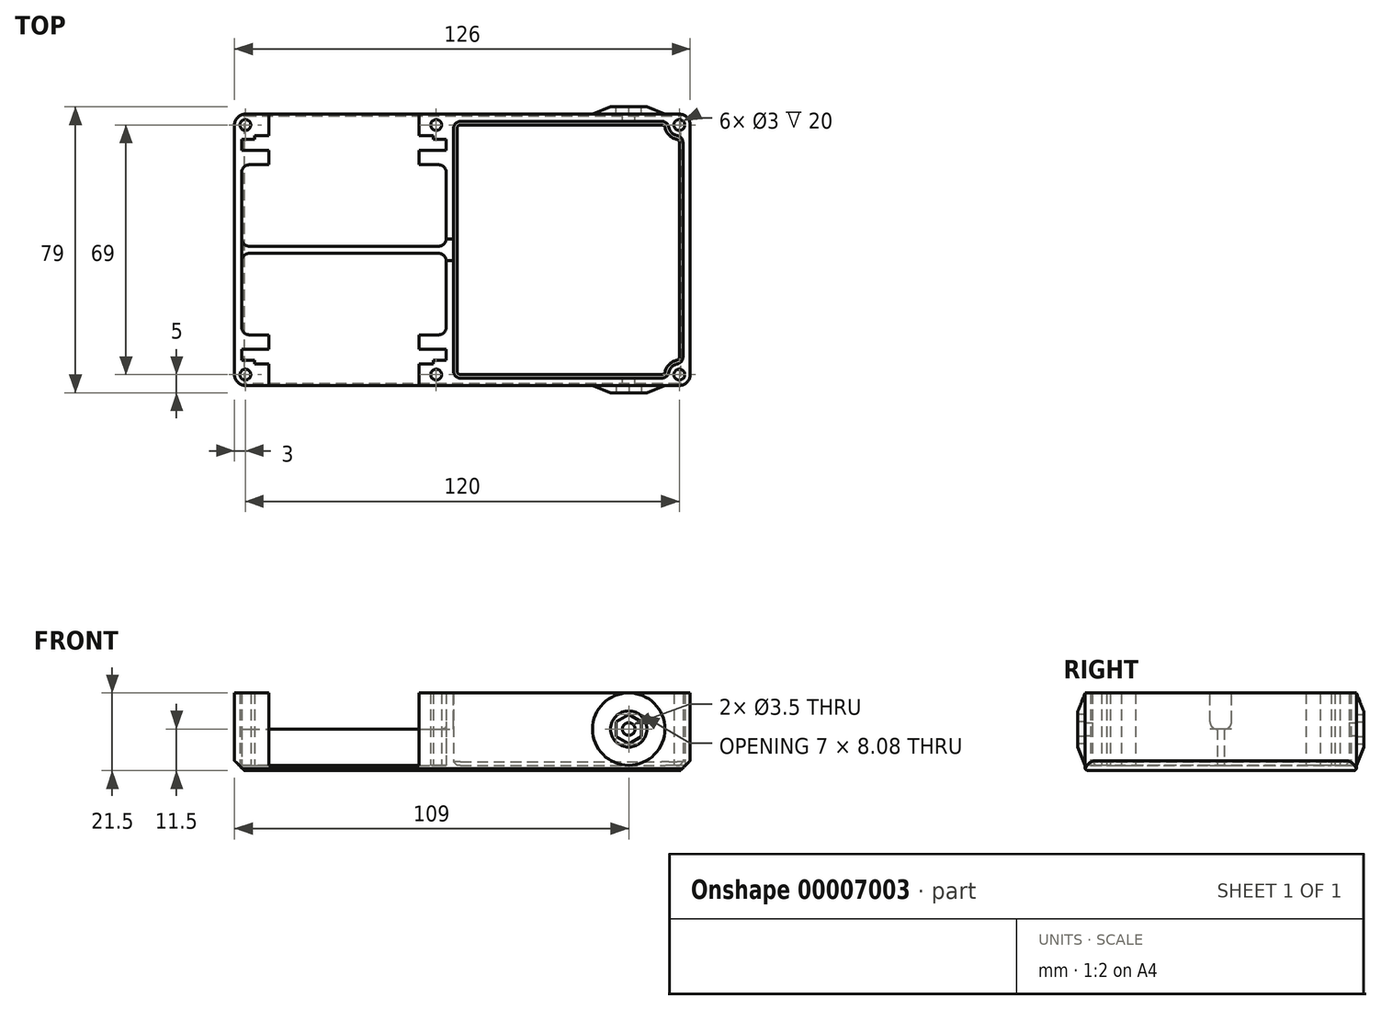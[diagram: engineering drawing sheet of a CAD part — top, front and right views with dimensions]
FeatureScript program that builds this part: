
annotation { "Feature Type Name" : "Feature", "Feature Type Description" : "" }
export const myFeature = defineFeature(function(context is Context, id is Id, definition is map)
    precondition{}
    {
        {
            var Q0;
            Q0=qCreatedBy(makeId("Top.planeOp"),FACE);
            var sketch = newSketch(context, id + "F0", { "sketchPlane" : qUnion([Q0])});
            skLineSegment(sketch, "E0.0", {"start": v(41, 72) * mm, "end": v(41, 66) * mm});
            skLineSegment(sketch, "E1.0", {"start": v(-7.5, 62) * mm, "end": v(-0.5, 62) * mm});
            skLineSegment(sketch, "E2.0", {"start": v(-8, 65) * mm, "end": v(-8, 62.5) * mm});
            skLineSegment(sketch, "E3.0", {"start": v(41, 62) * mm, "end": v(48, 62) * mm});
            skLineSegment(sketch, "E4.0", {"start": v(48.5, 62.5) * mm, "end": v(48.5, 65) * mm});
            skLineSegment(sketch, "E5.trimOffspring", {"start": v(-0.5, 66) * mm, "end": v(-0.5, 72) * mm});
            skLineSegment(sketch, "E6", {"start": v(-8, 62.5) * mm, "end": v(-8, 62) * mm});
            skLineSegment(sketch, "E7", {"start": v(-8, 62) * mm, "end": v(-7.5, 62) * mm});
            skLineSegment(sketch, "E8", {"start": v(48, 62) * mm, "end": v(48.5, 62) * mm});
            skLineSegment(sketch, "E9", {"start": v(48.5, 62) * mm, "end": v(48.5, 62.5) * mm});
            skLineSegment(sketch, "E10", {"start": v(45, 65) * mm, "end": v(48.5, 65) * mm});
            skLineSegment(sketch, "E11", {"start": v(-8, 65) * mm, "end": v(-4.5, 65) * mm});
            skLineSegment(sketch, "E12", {"start": v(-0.5, 66) * mm, "end": v(-4.5, 66) * mm});
            skLineSegment(sketch, "E13", {"start": v(-4.5, 66) * mm, "end": v(-4.5, 65) * mm});
            skLineSegment(sketch, "E14", {"start": v(41, 66) * mm, "end": v(45, 66) * mm});
            skLineSegment(sketch, "E15", {"start": v(45, 66) * mm, "end": v(45, 65) * mm});
            skLineSegment(sketch, "E16", {"start": v(-0.5, 62) * mm, "end": v(-0.5, 58) * mm});
            skLineSegment(sketch, "E17", {"start": v(41, 62) * mm, "end": v(41, 58) * mm});
            skLineSegment(sketch, "E18", {"start": v(-0.5, 58) * mm, "end": v(-8, 58) * mm});
            skLineSegment(sketch, "E19", {"start": v(41, 58) * mm, "end": v(48.5, 58) * mm});
            skLineSegment(sketch, "E20", {"start": v(-0.5, 72) * mm, "end": v(-10, 72) * mm});
            skLineSegment(sketch, "E21", {"start": v(41, 72) * mm, "end": v(116, 72) * mm});
            skLineSegment(sketch, "E22.1", {"start": v(50.5, 70) * mm, "end": v(110.17, 70) * mm});
            skPoint(sketch, "E23.endSnap0", {"position": v(41, 69) * mm});
            skCircle(sketch, "E24", {"center": v(45.75, 69) * mm, "radius": 1.5 * mm});
            skCircle(sketch, "E25", {"center": v(-7, 69) * mm, "radius": 1.5 * mm});
            skCircle(sketch, "E26", {"center": v(113, 69) * mm, "radius": 1.5 * mm});
            skArc(sketch, "E27.trimOffspring", {"start": v(110.17, 70) * mm, "mid": v(110.88, 66.88) * mm, "end": v(114, 66.17) * mm});
            skLineSegment(sketch, "E28", {"start": v(-8, 58) * mm, "end": v(-8, 35.5) * mm});
            skLineSegment(sketch, "E29", {"start": v(-8, 35.5) * mm, "end": v(48.5, 35.5) * mm});
            skLineSegment(sketch, "E30", {"start": v(48.5, 35.5) * mm, "end": v(48.5, 58) * mm});
            skLineSegment(sketch, "E31.MirrorCS", {"start": v(-8, 7) * mm, "end": v(-7.5, 7) * mm});
            skLineSegment(sketch, "E32.MirrorCS", {"start": v(48.5, 6.5) * mm, "end": v(48.5, 4) * mm});
            skLineSegment(sketch, "E33.MirrorCS", {"start": v(-8, 4) * mm, "end": v(-8, 6.5) * mm});
            skLineSegment(sketch, "E34.MirrorCS", {"start": v(-4.5, 3) * mm, "end": v(-4.5, 4) * mm});
            skLineSegment(sketch, "E35.MirrorCS", {"start": v(-0.5, 7) * mm, "end": v(-0.5, 11) * mm});
            skLineSegment(sketch, "E36.MirrorCS", {"start": v(-0.5, 3) * mm, "end": v(-4.5, 3) * mm});
            skCircle(sketch, "E37.MirrorC", {"center": v(113, 0) * mm, "radius": 1.5 * mm});
            skCircle(sketch, "E38.MirrorC", {"center": v(-7, 0) * mm, "radius": 1.5 * mm});
            skLineSegment(sketch, "E39.MirrorCS", {"start": v(45, 4) * mm, "end": v(48.5, 4) * mm});
            skLineSegment(sketch, "E40.MirrorCS", {"start": v(45, 3) * mm, "end": v(45, 4) * mm});
            skLineSegment(sketch, "E41.MirrorCS", {"start": v(-8, 4) * mm, "end": v(-4.5, 4) * mm});
            skLineSegment(sketch, "E42.MirrorCS", {"start": v(41, 7) * mm, "end": v(41, 11) * mm});
            skLineSegment(sketch, "E43.MirrorCS", {"start": v(41, 3) * mm, "end": v(45, 3) * mm});
            skLineSegment(sketch, "E44.MirrorCS", {"start": v(-0.5, -3) * mm, "end": v(-10, -3) * mm});
            skArc(sketch, "E45.MirrorCS", {"start": v(110.17, -1) * mm, "mid": v(110.88, 2.12) * mm, "end": v(114, 2.83) * mm});
            skCircle(sketch, "E46.MirrorC", {"center": v(45.75, 0) * mm, "radius": 1.5 * mm});
            skLineSegment(sketch, "E47.MirrorCS", {"start": v(-7.5, 7) * mm, "end": v(-0.5, 7) * mm});
            skLineSegment(sketch, "E48.MirrorCS", {"start": v(41, -3) * mm, "end": v(41, 3) * mm});
            skLineSegment(sketch, "E49.MirrorCS", {"start": v(-8, 33.5) * mm, "end": v(48.5, 33.5) * mm});
            skLineSegment(sketch, "E50.MirrorCS", {"start": v(41, 7) * mm, "end": v(48, 7) * mm});
            skLineSegment(sketch, "E51.MirrorCS", {"start": v(48.5, 33.5) * mm, "end": v(48.5, 11) * mm});
            skLineSegment(sketch, "E52.MirrorCS", {"start": v(-0.5, 3) * mm, "end": v(-0.5, -3) * mm});
            skPoint(sketch, "E53.MirrorP", {"position": v(41, 0) * mm});
            skLineSegment(sketch, "E54.MirrorCS", {"start": v(-0.5, 11) * mm, "end": v(-8, 11) * mm});
            skLineSegment(sketch, "E55.MirrorCS", {"start": v(41, 11) * mm, "end": v(48.5, 11) * mm});
            skLineSegment(sketch, "E56.MirrorCS", {"start": v(41, -3) * mm, "end": v(116, -3) * mm});
            skLineSegment(sketch, "E57.MirrorCS", {"start": v(-8, 11) * mm, "end": v(-8, 33.5) * mm});
            skLineSegment(sketch, "E58.MirrorCS", {"start": v(50.5, -1) * mm, "end": v(110.17, -1) * mm});
            skLineSegment(sketch, "E59", {"start": v(116, 72) * mm, "end": v(116, -3) * mm});
            skLineSegment(sketch, "E60", {"start": v(114, 2.83) * mm, "end": v(114, 66.17) * mm});
            skLineSegment(sketch, "E61", {"start": v(-10, 72) * mm, "end": v(-10, -3) * mm});
            skLineSegment(sketch, "E62", {"start": v(-8, 7) * mm, "end": v(-8, 6.5) * mm});
            skLineSegment(sketch, "E63", {"start": v(48, 7) * mm, "end": v(48.5, 7) * mm});
            skLineSegment(sketch, "E64", {"start": v(48.5, 7) * mm, "end": v(48.5, 6.5) * mm});
            skLineSegment(sketch, "E65", {"start": v(50.5, 70) * mm, "end": v(50.5, -1) * mm});
            skSolve(sketch);
        }
        {
            var Q0;
            Q0=makeQuery(id+"F0.imprint","IMPRINT",FACE,{"disambiguationData":[TD([[makeQuery(id+"F0.imprint","IMPRINT",EDGE,{"derivedFrom":sQuery(id+"F0.wireOp",EDGE,"E0.0")}),1.0]])]});
            extrude(context, id + "F1", {"entities" : qUnion([Q0]), "depth" : 20 * mm});
        }
        {
            var Q0;
            Q0=makeQuery(id+"F1.opExtrude","SWEPT_FACE",FACE,{"disambiguationData":[OSD([sQuery(id+"F0.wireOp",EDGE,"E21")])]});
            var sketch = newSketch(context, id + "F2", { "sketchPlane" : qUnion([Q0])});
            skCircle(sketch, "E66", {"center": v(-99, 10) * mm, "radius": 10 * mm});
            skPoint(sketch, "E66.centerSnap0", {"position": v(-113, 10) * mm});
            skSolve(sketch);
        }
        {
            var Q0;
            Q0 = qSketchRegion(id + "F2", true);
            extrude(context, id + "F3", {"entities" : qUnion([Q0]), "operationType" : NewBodyOperationType.ADD, "depth" : 2 * mm});
        }
        {
            var Q0;
            Q0=makeQuery(id+"F3.opExtrude","CAP_EDGE",EDGE,{"disambiguationData":[OSD([sQuery(id+"F2.wireOp",EDGE,"E66")])],"isStart":false});
            chamfer(context, id + "F4", {"entities" : qUnion([Q0]), "chamferType" : ChamferType.TWO_OFFSETS, "width1" : 5 * mm, "oppositeDirection" : false, "width2" : 2 * mm, "tangentPropagation" : true});
        }
        {
            var Q0;
            Q0=makeQuery(id+"F3.opExtrude","CAP_FACE",FACE,{"disambiguationData":[OSD([sQuery(id+"F2.wireOp",EDGE,"E66")])],"isStart":false});
            var sketch = newSketch(context, id + "F5", { "sketchPlane" : qUnion([Q0])});
            skCircle(sketch, "E67", {"center": v(-99, 10) * mm, "radius": 1.75 * mm});
            skSolve(sketch);
        }
        {
            var Q0;
            Q0=makeQuery(id+"F1.opExtrude","SWEPT_FACE",FACE,{"disambiguationData":[OSD([sQuery(id+"F0.wireOp",EDGE,"E56.MirrorCS")])]});
            var sketch = newSketch(context, id + "F6", { "sketchPlane" : qUnion([Q0])});
            skCircle(sketch, "E68", {"center": v(99, 10) * mm, "radius": 10 * mm});
            skSolve(sketch);
        }
        {
            var Q0;
            Q0 = qSketchRegion(id + "F6", true);
            extrude(context, id + "F7", {"entities" : qUnion([Q0]), "operationType" : NewBodyOperationType.ADD, "depth" : 2 * mm});
        }
        {
            var Q0;
            Q0=makeQuery(id+"F5.imprint","IMPRINT",FACE,{"disambiguationData":[TD([[makeQuery(id+"F5.imprint","IMPRINT",EDGE,{"derivedFrom":sQuery(id+"F5.wireOp",EDGE,"E67")}),1.0]])]});
            extrude(context, id + "F8", {"entities" : qUnion([Q0]), "operationType" : NewBodyOperationType.REMOVE, "oppositeDirection" : true, "depth" : 100 * mm});
        }
        {
            var Q0;
            Q0=makeQuery(id+"F7.opExtrude","CAP_EDGE",EDGE,{"disambiguationData":[OSD([sQuery(id+"F6.wireOp",EDGE,"E68")])],"isStart":false});
            chamfer(context, id + "F9", {"entities" : qUnion([Q0]), "chamferType" : ChamferType.TWO_OFFSETS, "width1" : 5 * mm, "oppositeDirection" : false, "width2" : 2 * mm, "tangentPropagation" : true});
        }
        {
            var Q0;
            Q0=makeQuery(id+"F1.opExtrude","SWEPT_EDGE",EDGE,{"disambiguationData":[OSD([sQuery(id+"F0.wireOp",EDGE,"E44.MirrorCS"),sQuery(id+"F0.wireOp",EDGE,"E61")])]});
            var Q1;
            Q1=makeQuery(id+"F1.opExtrude","SWEPT_EDGE",EDGE,{"disambiguationData":[OSD([sQuery(id+"F0.wireOp",EDGE,"E56.MirrorCS"),sQuery(id+"F0.wireOp",EDGE,"E59")])]});
            var Q2;
            Q2=makeQuery(id+"F1.opExtrude","SWEPT_EDGE",EDGE,{"disambiguationData":[OSD([sQuery(id+"F0.wireOp",EDGE,"E21"),sQuery(id+"F0.wireOp",EDGE,"E59")])]});
            var Q3;
            Q3=makeQuery(id+"F1.opExtrude","SWEPT_EDGE",EDGE,{"disambiguationData":[OSD([sQuery(id+"F0.wireOp",EDGE,"E20"),sQuery(id+"F0.wireOp",EDGE,"E61")])]});
            fillet(context, id + "F10", {"entities" : qUnion([Q0, Q1, Q2, Q3]), "radius" : 3 * mm, "tangentPropagation" : true, "allowEdgeOverflow" : false});
        }
        {
            var Q0;
            Q0=makeQuery(id+"F1.opExtrude","SWEPT_EDGE",EDGE,{"disambiguationData":[OSD([sQuery(id+"F0.wireOp",EDGE,"E45.MirrorCS"),sQuery(id+"F0.wireOp",EDGE,"E58.MirrorCS")])]});
            var Q1;
            Q1=makeQuery(id+"F1.opExtrude","SWEPT_EDGE",EDGE,{"disambiguationData":[OSD([sQuery(id+"F0.wireOp",EDGE,"E45.MirrorCS"),sQuery(id+"F0.wireOp",EDGE,"E60")])]});
            var Q2;
            Q2=makeQuery(id+"F1.opExtrude","SWEPT_EDGE",EDGE,{"disambiguationData":[OSD([sQuery(id+"F0.wireOp",EDGE,"E58.MirrorCS"),sQuery(id+"F0.wireOp",EDGE,"E65")])]});
            var Q3;
            Q3=makeQuery(id+"F1.opExtrude","SWEPT_EDGE",EDGE,{"disambiguationData":[OSD([sQuery(id+"F0.wireOp",EDGE,"E22.1"),sQuery(id+"F0.wireOp",EDGE,"E65")])]});
            var Q4;
            Q4=makeQuery(id+"F1.opExtrude","SWEPT_EDGE",EDGE,{"disambiguationData":[OSD([sQuery(id+"F0.wireOp",EDGE,"E22.1"),sQuery(id+"F0.wireOp",EDGE,"E27.trimOffspring")])]});
            var Q5;
            Q5=makeQuery(id+"F1.opExtrude","SWEPT_EDGE",EDGE,{"disambiguationData":[OSD([sQuery(id+"F0.wireOp",EDGE,"E27.trimOffspring"),sQuery(id+"F0.wireOp",EDGE,"E60")])]});
            var Q6;
            Q6=makeQuery(id+"F1.opExtrude","SWEPT_EDGE",EDGE,{"disambiguationData":[OSD([sQuery(id+"F0.wireOp",EDGE,"E49.MirrorCS"),sQuery(id+"F0.wireOp",EDGE,"E57.MirrorCS")])]});
            var Q7;
            Q7=makeQuery(id+"F1.opExtrude","SWEPT_EDGE",EDGE,{"disambiguationData":[OSD([sQuery(id+"F0.wireOp",EDGE,"E28"),sQuery(id+"F0.wireOp",EDGE,"E29")])]});
            var Q8;
            Q8=makeQuery(id+"F1.opExtrude","SWEPT_EDGE",EDGE,{"disambiguationData":[OSD([sQuery(id+"F0.wireOp",EDGE,"E29"),sQuery(id+"F0.wireOp",EDGE,"E30")])]});
            var Q9;
            Q9=makeQuery(id+"F1.opExtrude","SWEPT_EDGE",EDGE,{"disambiguationData":[OSD([sQuery(id+"F0.wireOp",EDGE,"E49.MirrorCS"),sQuery(id+"F0.wireOp",EDGE,"E51.MirrorCS")])]});
            var Q10;
            Q10=makeQuery(id+"F1.opExtrude","SWEPT_EDGE",EDGE,{"disambiguationData":[OSD([sQuery(id+"F0.wireOp",EDGE,"E19"),sQuery(id+"F0.wireOp",EDGE,"E30")])]});
            var Q11;
            Q11=makeQuery(id+"F1.opExtrude","SWEPT_EDGE",EDGE,{"disambiguationData":[OSD([sQuery(id+"F0.wireOp",EDGE,"E18"),sQuery(id+"F0.wireOp",EDGE,"E28")])]});
            var Q12;
            Q12=makeQuery(id+"F1.opExtrude","SWEPT_EDGE",EDGE,{"disambiguationData":[OSD([sQuery(id+"F0.wireOp",EDGE,"E54.MirrorCS"),sQuery(id+"F0.wireOp",EDGE,"E57.MirrorCS")])]});
            var Q13;
            Q13=makeQuery(id+"F1.opExtrude","SWEPT_EDGE",EDGE,{"disambiguationData":[OSD([sQuery(id+"F0.wireOp",EDGE,"E51.MirrorCS"),sQuery(id+"F0.wireOp",EDGE,"E55.MirrorCS")])]});
            fillet(context, id + "F11", {"entities" : qUnion([Q0, Q1, Q2, Q3, Q4, Q5, Q6, Q7, Q8, Q9, Q10, Q11, Q12, Q13]), "radius" : 2 * mm, "tangentPropagation" : true, "allowEdgeOverflow" : false});
        }
        {
            var Q0;
            Q0=makeQuery(id+"F3.opExtrude","CAP_FACE",FACE,{"disambiguationData":[OSD([sQuery(id+"F2.wireOp",EDGE,"E66")])],"isStart":false});
            var sketch = newSketch(context, id + "F12", { "sketchPlane" : qUnion([Q0])});
            skCircle(sketch, "E69.cCircle", {"center": v(-99, 10) * mm, "radius": 3.5 * mm, "construction": true});
            skLineSegment(sketch, "E69.0", {"start": v(-95.5, 12.02) * mm, "end": v(-95.5, 7.98) * mm});
            skLineSegment(sketch, "E69.1", {"start": v(-95.5, 7.98) * mm, "end": v(-99, 5.96) * mm});
            skLineSegment(sketch, "E69.2", {"start": v(-99, 5.96) * mm, "end": v(-102.5, 7.98) * mm});
            skLineSegment(sketch, "E69.3", {"start": v(-102.5, 7.98) * mm, "end": v(-102.5, 12.02) * mm});
            skLineSegment(sketch, "E69.4", {"start": v(-102.5, 12.02) * mm, "end": v(-99, 14.04) * mm});
            skLineSegment(sketch, "E69.5", {"start": v(-99, 14.04) * mm, "end": v(-95.5, 12.02) * mm});
            skPoint(sketch, "E69.0.midPoint", {"position": v(-95.5, 10) * mm});
            skSolve(sketch);
        }
        {
            var Q0;
            Q0=makeQuery(id+"F12.imprint","IMPRINT",FACE,{"disambiguationData":[TD([[makeQuery(id+"F12.imprint","IMPRINT",EDGE,{"derivedFrom":sQuery(id+"F12.wireOp",EDGE,"E69.0")}),-1.0]])]});
            extrude(context, id + "F13", {"entities" : qUnion([Q0]), "operationType" : NewBodyOperationType.REMOVE, "oppositeDirection" : true, "depth" : 2 * mm});
        }
        {
            var Q0;
            Q0=makeQuery(id+"F7.opExtrude","CAP_FACE",FACE,{"disambiguationData":[OSD([sQuery(id+"F6.wireOp",EDGE,"E68")])],"isStart":false});
            var sketch = newSketch(context, id + "F14", { "sketchPlane" : qUnion([Q0])});
            skCircle(sketch, "E70.cCircle", {"center": v(99, 10) * mm, "radius": 3.5 * mm, "construction": true});
            skLineSegment(sketch, "E70.0", {"start": v(95.5, 7.98) * mm, "end": v(95.5, 12.02) * mm});
            skLineSegment(sketch, "E70.1", {"start": v(95.5, 12.02) * mm, "end": v(99, 14.04) * mm});
            skLineSegment(sketch, "E70.2", {"start": v(99, 14.04) * mm, "end": v(102.5, 12.02) * mm});
            skLineSegment(sketch, "E70.3", {"start": v(102.5, 12.02) * mm, "end": v(102.5, 7.98) * mm});
            skLineSegment(sketch, "E70.4", {"start": v(102.5, 7.98) * mm, "end": v(99, 5.96) * mm});
            skLineSegment(sketch, "E70.5", {"start": v(99, 5.96) * mm, "end": v(95.5, 7.98) * mm});
            skPoint(sketch, "E70.0.midPoint", {"position": v(95.5, 10) * mm});
            skSolve(sketch);
        }
        {
            var Q0;
            Q0 = qSketchRegion(id + "F14", true);
            extrude(context, id + "F15", {"entities" : qUnion([Q0]), "operationType" : NewBodyOperationType.REMOVE, "oppositeDirection" : true, "depth" : 2 * mm});
        }
        {
            var Q0;
            Q0=makeQuery(id+"F1.opExtrude","CAP_FACE",FACE,{"disambiguationData":[OSD([sQuery(id+"F0.wireOp",EDGE,"E0.0"),sQuery(id+"F0.wireOp",EDGE,"E1.0"),sQuery(id+"F0.wireOp",EDGE,"E2.0"),sQuery(id+"F0.wireOp",EDGE,"E3.0"),sQuery(id+"F0.wireOp",EDGE,"E4.0"),sQuery(id+"F0.wireOp",EDGE,"E5.trimOffspring"),sQuery(id+"F0.wireOp",EDGE,"E6"),sQuery(id+"F0.wireOp",EDGE,"E7"),sQuery(id+"F0.wireOp",EDGE,"E8"),sQuery(id+"F0.wireOp",EDGE,"E9"),sQuery(id+"F0.wireOp",EDGE,"E10"),sQuery(id+"F0.wireOp",EDGE,"E11"),sQuery(id+"F0.wireOp",EDGE,"E12"),sQuery(id+"F0.wireOp",EDGE,"E13"),sQuery(id+"F0.wireOp",EDGE,"E14"),sQuery(id+"F0.wireOp",EDGE,"E15"),sQuery(id+"F0.wireOp",EDGE,"E16"),sQuery(id+"F0.wireOp",EDGE,"E17"),sQuery(id+"F0.wireOp",EDGE,"E18"),sQuery(id+"F0.wireOp",EDGE,"E19"),sQuery(id+"F0.wireOp",EDGE,"E20"),sQuery(id+"F0.wireOp",EDGE,"E21"),sQuery(id+"F0.wireOp",EDGE,"E22.1"),sQuery(id+"F0.wireOp",EDGE,"E24"),sQuery(id+"F0.wireOp",EDGE,"E25"),sQuery(id+"F0.wireOp",EDGE,"E26"),sQuery(id+"F0.wireOp",EDGE,"E27.trimOffspring"),sQuery(id+"F0.wireOp",EDGE,"E28"),sQuery(id+"F0.wireOp",EDGE,"E29"),sQuery(id+"F0.wireOp",EDGE,"E30"),sQuery(id+"F0.wireOp",EDGE,"E31.MirrorCS"),sQuery(id+"F0.wireOp",EDGE,"E32.MirrorCS"),sQuery(id+"F0.wireOp",EDGE,"E33.MirrorCS"),sQuery(id+"F0.wireOp",EDGE,"E34.MirrorCS"),sQuery(id+"F0.wireOp",EDGE,"E35.MirrorCS"),sQuery(id+"F0.wireOp",EDGE,"E36.MirrorCS"),sQuery(id+"F0.wireOp",EDGE,"E37.MirrorC"),sQuery(id+"F0.wireOp",EDGE,"E38.MirrorC"),sQuery(id+"F0.wireOp",EDGE,"E39.MirrorCS"),sQuery(id+"F0.wireOp",EDGE,"E40.MirrorCS"),sQuery(id+"F0.wireOp",EDGE,"E41.MirrorCS"),sQuery(id+"F0.wireOp",EDGE,"E42.MirrorCS"),sQuery(id+"F0.wireOp",EDGE,"E43.MirrorCS"),sQuery(id+"F0.wireOp",EDGE,"E44.MirrorCS"),sQuery(id+"F0.wireOp",EDGE,"E45.MirrorCS"),sQuery(id+"F0.wireOp",EDGE,"E46.MirrorC"),sQuery(id+"F0.wireOp",EDGE,"E47.MirrorCS"),sQuery(id+"F0.wireOp",EDGE,"E48.MirrorCS"),sQuery(id+"F0.wireOp",EDGE,"E49.MirrorCS"),sQuery(id+"F0.wireOp",EDGE,"E50.MirrorCS"),sQuery(id+"F0.wireOp",EDGE,"E51.MirrorCS"),sQuery(id+"F0.wireOp",EDGE,"E52.MirrorCS"),sQuery(id+"F0.wireOp",EDGE,"E54.MirrorCS"),sQuery(id+"F0.wireOp",EDGE,"E55.MirrorCS"),sQuery(id+"F0.wireOp",EDGE,"E56.MirrorCS"),sQuery(id+"F0.wireOp",EDGE,"E57.MirrorCS"),sQuery(id+"F0.wireOp",EDGE,"E58.MirrorCS"),sQuery(id+"F0.wireOp",EDGE,"E59"),sQuery(id+"F0.wireOp",EDGE,"E60"),sQuery(id+"F0.wireOp",EDGE,"E61"),sQuery(id+"F0.wireOp",EDGE,"E62"),sQuery(id+"F0.wireOp",EDGE,"E63"),sQuery(id+"F0.wireOp",EDGE,"E64"),sQuery(id+"F0.wireOp",EDGE,"E65")])],"isStart":false});
            var sketch = newSketch(context, id + "F16", { "sketchPlane" : qUnion([Q0])});
            skLineSegment(sketch, "E71", {"start": v(-8, 37.5) * mm, "end": v(-8, 31.5) * mm});
            skLineSegment(sketch, "E72", {"start": v(-8, 31.5) * mm, "end": v(48.5, 31.5) * mm});
            skLineSegment(sketch, "E73", {"start": v(48.5, 37.5) * mm, "end": v(-8, 37.5) * mm});
            skLineSegment(sketch, "E74", {"start": v(48.5, 37.5) * mm, "end": v(50.5, 37.5) * mm});
            skLineSegment(sketch, "E75", {"start": v(50.5, 37.5) * mm, "end": v(50.5, 31.5) * mm});
            skLineSegment(sketch, "E76", {"start": v(50.5, 31.5) * mm, "end": v(48.5, 31.5) * mm});
            skSolve(sketch);
        }
        {
            var Q0;
            Q0 = qSketchRegion(id + "F16", true);
            extrude(context, id + "F17", {"entities" : qUnion([Q0]), "operationType" : NewBodyOperationType.REMOVE, "oppositeDirection" : true, "depth" : 10 * mm});
        }
        {
            var Q0;
            Q0=makeQuery(id+"F17.boolean.opBoolean","COPY",EDGE,{"derivedFrom":makeQuery(id+"F17.opExtrude","CAP_EDGE",EDGE,{"disambiguationData":[OSD([sQuery(id+"F16.wireOp",EDGE,"E73"),sQuery(id+"F16.wireOp",EDGE,"E74")])],"isStart":false})});
            var Q1;
            Q1=makeQuery(id+"F17.boolean.opBoolean","COPY",EDGE,{"derivedFrom":makeQuery(id+"F17.opExtrude","CAP_EDGE",EDGE,{"disambiguationData":[OSD([sQuery(id+"F16.wireOp",EDGE,"E72"),sQuery(id+"F16.wireOp",EDGE,"E76")])],"isStart":false})});
            fillet(context, id + "F18", {"entities" : qUnion([Q0, Q1]), "radius" : 2 * mm, "tangentPropagation" : true, "allowEdgeOverflow" : false});
        }
        {
            var Q0;
            Q0=qCreatedBy(makeId("Top.planeOp"),FACE);
            var sketch = newSketch(context, id + "F19", { "sketchPlane" : qUnion([Q0])});
            skArc(sketch, "E77.0", {"start": v(-10, 0) * mm, "mid": v(-9.12, -2.12) * mm, "end": v(-7, -3) * mm});
            skArc(sketch, "E77.1", {"start": v(-7, 72) * mm, "mid": v(-9.12, 71.12) * mm, "end": v(-10, 69) * mm});
            skArc(sketch, "E77.2", {"start": v(116, 69) * mm, "mid": v(115.12, 71.12) * mm, "end": v(113, 72) * mm});
            skArc(sketch, "E77.3", {"start": v(113, -3) * mm, "mid": v(115.12, -2.12) * mm, "end": v(116, 0) * mm});
            skLineSegment(sketch, "E78", {"start": v(-7, 72) * mm, "end": v(113, 72) * mm});
            skLineSegment(sketch, "E79", {"start": v(116, 69) * mm, "end": v(116, 0) * mm});
            skLineSegment(sketch, "E80", {"start": v(113, -3) * mm, "end": v(-7, -3) * mm});
            skLineSegment(sketch, "E81", {"start": v(-10, 0) * mm, "end": v(-10, 69) * mm});
            skSolve(sketch);
        }
        {
            var Q0;
            Q0 = qSketchRegion(id + "F19", true);
            extrude(context, id + "F20", {"entities" : qUnion([Q0]), "operationType" : NewBodyOperationType.ADD, "oppositeDirection" : true, "depth" : 1.5 * mm});
        }
        {
            var Q0;
            Q0=makeQuery(id+"F20.opExtrude","CAP_EDGE",EDGE,{"disambiguationData":[OSD([sQuery(id+"F19.wireOp",EDGE,"E81")])],"isStart":false});
            var Q1;
            Q1=makeQuery(id+"F20.opExtrude","CAP_EDGE",EDGE,{"disambiguationData":[OSD([sQuery(id+"F19.wireOp",EDGE,"E79")])],"isStart":false});
            chamfer(context, id + "F21", {"entities" : qUnion([Q0, Q1]), "width" : 2.75 * mm});
        }
        {
            var Q0;
            {var subQ3=sQuery(id+"F0.wireOp",EDGE,"E22.1");Q0=makeQuery(id+"F20.boolean.opBoolean","SPLIT",FACE,{"disambiguationData":[TD([makeQuery(id+"F1.opExtrude","SWEPT_FACE",FACE,{"disambiguationData":[OSD([subQ3])]})])],"derivedFrom":makeQuery(id+"F20.opExtrude","CAP_FACE",FACE,{"disambiguationData":[OSD([sQuery(id+"F19.wireOp",EDGE,"E77.0"),sQuery(id+"F19.wireOp",EDGE,"E77.1"),sQuery(id+"F19.wireOp",EDGE,"E77.2"),sQuery(id+"F19.wireOp",EDGE,"E77.3"),sQuery(id+"F19.wireOp",EDGE,"E78"),sQuery(id+"F19.wireOp",EDGE,"E79"),sQuery(id+"F19.wireOp",EDGE,"E80"),sQuery(id+"F19.wireOp",EDGE,"E81")])],"isStart":true})});}
            chamfer(context, id + "F22", {"entities" : qUnion([Q0]), "width" : 1 * mm, "tangentPropagation" : true});
        }
        {
            var Q0;
            Q0=makeQuery(id+"F20.opExtrude","CAP_EDGE",EDGE,{"disambiguationData":[OSD([sQuery(id+"F19.wireOp",EDGE,"E80")])],"isStart":false});
            var Q1;
            Q1=makeQuery(id+"F20.opExtrude","CAP_EDGE",EDGE,{"disambiguationData":[OSD([sQuery(id+"F19.wireOp",EDGE,"E78")])],"isStart":false});
            chamfer(context, id + "F23", {"entities" : qUnion([Q0, Q1]), "width" : .5 * mm, "tangentPropagation" : true});
        }
    });
